# Revit family: RN 15132 Valvola di ritegno EA
name_source: partatom
category: Rohrzubehör
units: mm (PartAtom-declared; Revit-internal decimal feet)

## family parameters
Arbeitsebenenbasiert = Nein
Beim Laden mit Abzugskörper schneiden = Nein
Bemaßung runder Anschluss = Durchmesser verwenden
Gemeinsam genutzt = Nein
Immer vertikal = Ja
Teiletyp = Ventil - Zerlegung in

## types (4) — shared parameters
1.010.00.2 Blattnummer der Richtlinie = 17
1.010.00.3 Ausgabedatum (Monat) der Richtlinie = 201601
1.010.00.4 Herstellername = R. Nussbaum AG
1.010.00.5 Revisionsdatum der Datei = 20190528
1.010.00.6 Webadresse des Herstellers = http://www.nussbaum.ch
1.100.00.3 Sortiernummer für Anzeigereihenfolge = 4
1.100.00.4 Produktbezeichnung = Sicherungs- und Ringleitungsarmaturen
1.960/3L.00.8 Link (URL) = https://www.nussbaum.ch
17.700.00.4 Armaturentyp = 6
17.700.00.7 Maximale Betriebstemperatur TB [°C] = 90
17.700.00.8 Maximaler Betriebsdruck (Arbeitsdruck) ps [1.0 · 105 Pa] = 16
Connector Visibility = Nein
EnclosingSpace Visibility = Nein
Hersteller = R. Nussbauzm AG
URL = https://www.nussbaum.ch

## per-type parameters (varying)
| type | 1.800.00.3 TGA-Nummer | 1.810.00.3 Hersteller-Bestellnummer | 1.810.00.4 DATANORM-Nummer | 1.810.00.5 StLB-Nummer | 1.810.00.6 GTIN-Nummer | 17.700.00.30 Produktbeschreibung | 17.700.00.5 Nennweite DN | 17.700.00.6 kvs-Wert [m3/h] | CONNECTOR0_DIAMETER_dX_0r | CONNECTOR0_dX_00 | CONNECTOR0_dX_01 | CONNECTOR0_ref_dX | CONNECTOR1_DIAMETER_dX_0r | CONNECTOR1_dX_00 | CONNECTOR1_dX_01 | CONNECTOR1_ref_dX | Modell | R. Nussbaum AG 15132.21 de Visibility | R. Nussbaum AG 15132.27 de Visibility | R. Nussbaum AG 15132.28 de Visibility | R. Nussbaum AG 15132.29 de Visibility | Typenkommentare |
| DN 65 | 00401700000000000000000000000200700000000000000001???00000 | 15132.27 | 15132.27 | 714.117 | 7612945726346 | 15132.27, Rückflussverhinderer EA, mit Flanschen, DN=65 | 65 | 120 | 65 mm | 145 mm | 130 mm | 130 mm | 65 mm | 130 mm | 145 mm | 130 mm | 15132.27 | Nein | Ja | Nein | Nein | Valvola di ritegno EADN 65 |
| DN 80 | 00401700000000000000000000000200700000000000000002???00000 | 15132.28 | 15132.28 | 714.118 | 7612945726353 | 15132.28, Rückflussverhinderer EA, mit Flanschen, DN=80 | 80 | 180 | 80 mm | 155 mm | 137 mm | 137 mm | 80 mm | 137 mm | 155 mm | 137 mm | 15132.28 | Nein | Nein | Ja | Nein | Valvola di ritegno EADN 80 |
| DN 100 | 00401700000000000000000000000200700000000000000003???00000 | 15132.29 | 15132.29 | 714.121 | 7612945726360 | 15132.29, Rückflussverhinderer EA, mit Flanschen, DN=100 | 100 | 294 | 100 mm  [stored 0.328084 ft] | 175 mm | 155 mm | 155 mm | 100 mm  [stored 0.328084 ft] | 155 mm | 175 mm | 155 mm | 15132.29 | Nein | Nein | Nein | Ja | Valvola di ritegno EADN 100 |
| DN 50 | 00401900000000000000000000000200700000000000000001???00000 | 15132.21 | 15132.21 | 714.116 | 7612945734068 | 15132.21, Rückflussverhinderer EA, mit Flanschen, DN=50 | 50 | 61 | 50 mm | 115 mm | 100 mm  [stored 0.328084 ft] | 100 mm  [stored 0.328084 ft] | 50 mm | 100 mm  [stored 0.328084 ft] | 115 mm | 100 mm  [stored 0.328084 ft] | 15132.21 | Ja | Nein | Nein | Nein | Valvola di ritegno EADN 50 |

note: [stored X ft] marks values corroborated as IEEE doubles in the binary element streams (Revit-internal decimal feet)

## geometry (parser evidence)
native form markers: Sweep x1
no freeform markers — native parametric forms only
